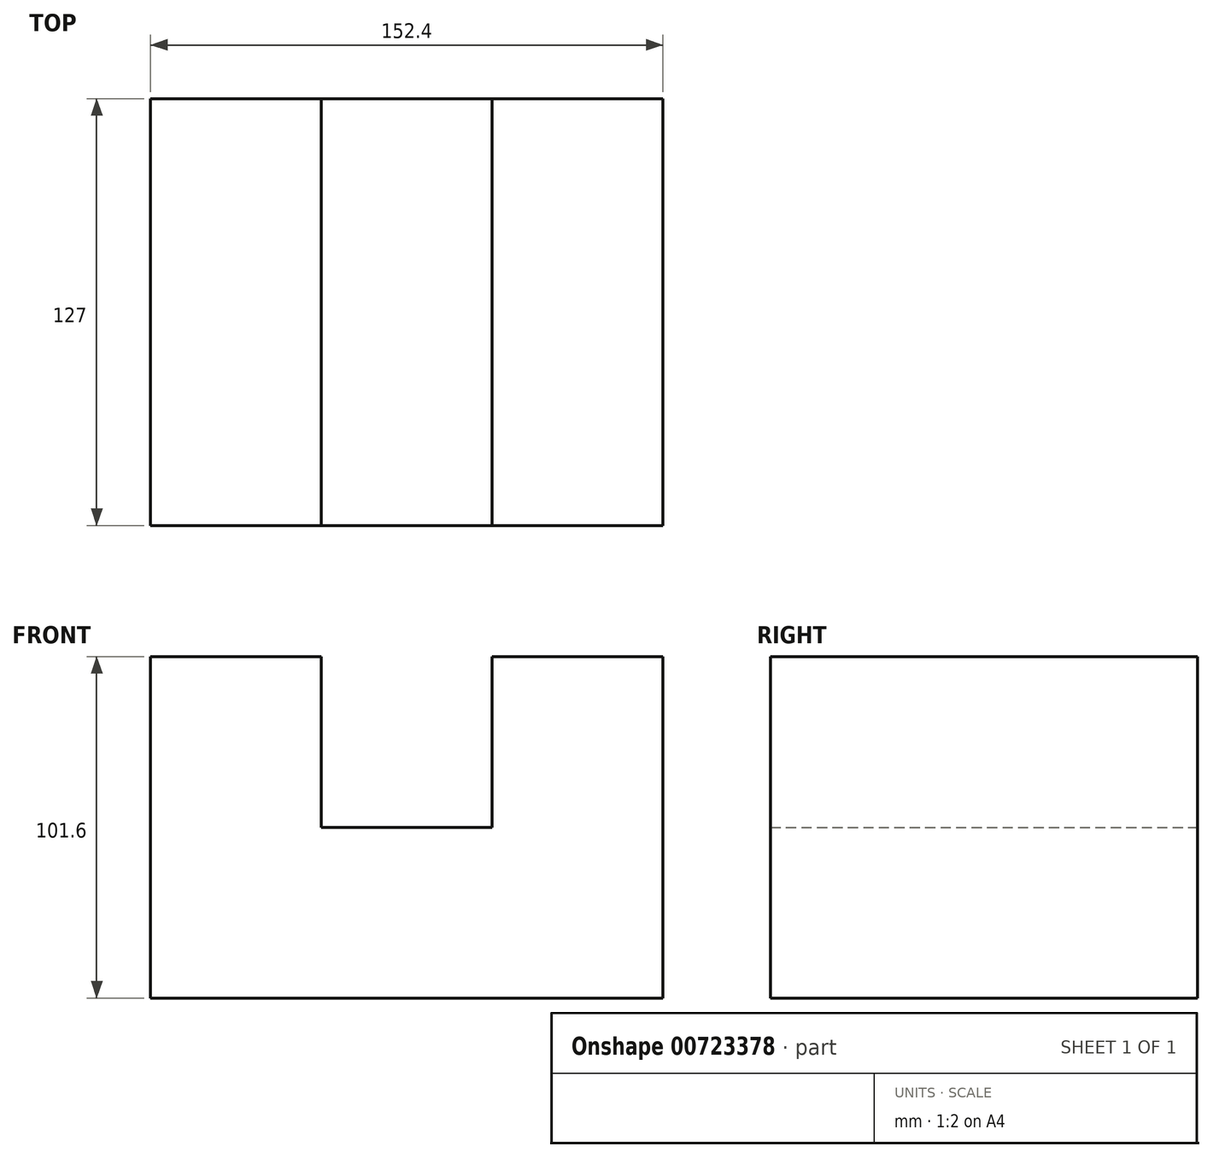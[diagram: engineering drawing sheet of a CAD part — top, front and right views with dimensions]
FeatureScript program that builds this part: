
annotation { "Feature Type Name" : "Feature", "Feature Type Description" : "" }
export const myFeature = defineFeature(function(context is Context, id is Id, definition is map)
    precondition{}
    {
        {
            var Q0;
            Q0=qCreatedBy(makeId("Front.planeOp"),FACE);
            var sketch = newSketch(context, id + "F0", { "sketchPlane" : qUnion([Q0])});
            skLineSegment(sketch, "E0", {"start": v(-151.11, -101.6) * mm, "end": v(1.29, -101.6) * mm});
            skLineSegment(sketch, "E1", {"start": v(-151.11, -101.6) * mm, "end": v(-151.11, 0) * mm});
            skLineSegment(sketch, "E2", {"start": v(1.29, -101.6) * mm, "end": v(1.29, 0) * mm});
            skLineSegment(sketch, "E3", {"start": v(-151.11, 0) * mm, "end": v(-100.31, 0) * mm});
            skLineSegment(sketch, "E4", {"start": v(-100.31, 0) * mm, "end": v(-100.31, -50.8) * mm});
            skLineSegment(sketch, "E5", {"start": v(-100.31, -50.8) * mm, "end": v(-49.51, -50.8) * mm});
            skLineSegment(sketch, "E6", {"start": v(-49.51, -50.8) * mm, "end": v(-49.51, 0) * mm});
            skLineSegment(sketch, "E7", {"start": v(-49.51, 0) * mm, "end": v(1.29, 0) * mm});
            skSolve(sketch);
        }
        {
            var Q0;
            Q0=makeQuery(id+"F0.imprint","IMPRINT",FACE,{"disambiguationData":[TD([[makeQuery(id+"F0.imprint","IMPRINT",EDGE,{"derivedFrom":sQuery(id+"F0.wireOp",EDGE,"E0")}),1.0]])]});
            extrude(context, id + "F1", {"entities" : qUnion([Q0]), "depth" : 127 * mm, "offsetDistance" : 25.4 * mm});
        }
    });
